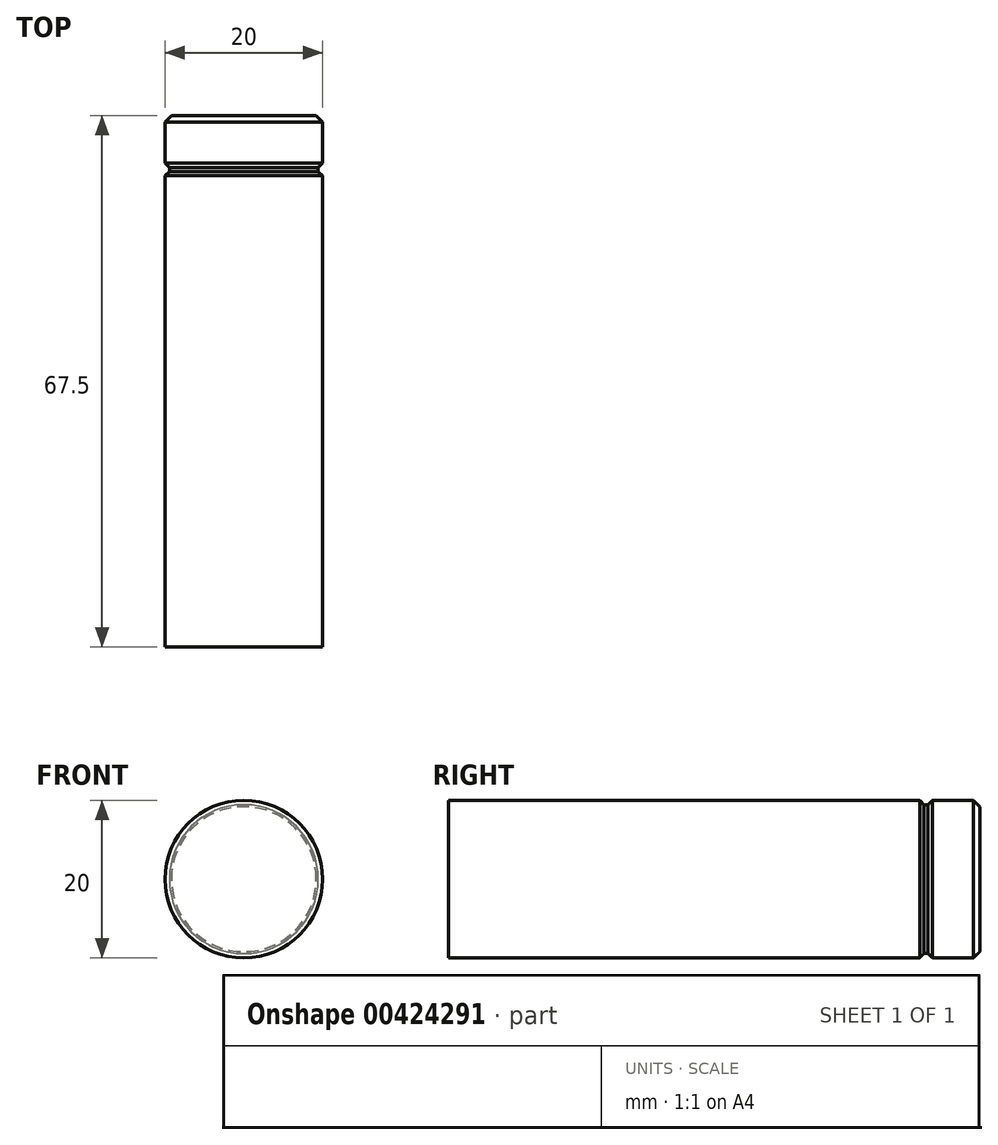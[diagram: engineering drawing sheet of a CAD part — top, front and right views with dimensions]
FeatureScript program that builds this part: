
annotation { "Feature Type Name" : "Feature", "Feature Type Description" : "" }
export const myFeature = defineFeature(function(context is Context, id is Id, definition is map)
    precondition{}
    {
        {
            var Q0;
            Q0=qCreatedBy(makeId("Front.planeOp"),FACE);
            var sketch = newSketch(context, id + "F0", { "sketchPlane" : qUnion([Q0])});
            skCircle(sketch, "E0", {"center": v(0, 0) * mm, "radius": 10 * mm});
            skSolve(sketch);
        }
        {
            var Q0;
            Q0=makeQuery(id+"F0.imprint","IMPRINT",FACE,{"disambiguationData":[TD([[makeQuery(id+"F0.imprint","IMPRINT",EDGE,{"derivedFrom":sQuery(id+"F0.wireOp",EDGE,"E0")}),1.0]])]});
            extrude(context, id + "F1", {"entities" : qUnion([Q0]), "oppositeDirection" : true, "depth" : 67.5 * mm});
        }
        {
            var Q0;
            Q0=qCreatedBy(makeId("Right.planeOp"),FACE);
            var sketch = newSketch(context, id + "F2", { "sketchPlane" : qUnion([Q0])});
            skLineSegment(sketch, "E1.bottom", {"start": v(60.9, 9.46) * mm, "end": v(60.4, 9.46) * mm});
            skLineSegment(sketch, "E2", {"start": v(60.4, 9.46) * mm, "end": v(59.83, 10.02) * mm});
            skLineSegment(sketch, "E3", {"start": v(60.9, 9.46) * mm, "end": v(61.47, 10.02) * mm});
            skLineSegment(sketch, "E4", {"start": v(61.47, 10.02) * mm, "end": v(59.83, 10.02) * mm});
            skLineSegment(sketch, "E5.MirrorCS", {"start": v(60.9, -9.46) * mm, "end": v(60.4, -9.46) * mm});
            skLineSegment(sketch, "E6.MirrorCS", {"start": v(61.47, -10.02) * mm, "end": v(59.83, -10.02) * mm});
            skLineSegment(sketch, "E7.MirrorCS", {"start": v(60.9, -9.46) * mm, "end": v(61.47, -10.02) * mm});
            skLineSegment(sketch, "E8.MirrorCS", {"start": v(60.4, -9.46) * mm, "end": v(59.83, -10.02) * mm});
            skSolve(sketch);
        }
        {
            var Q0;
            Q0=makeQuery(id+"F2.imprint","IMPRINT",FACE,{"disambiguationData":[TD([[makeQuery(id+"F2.imprint","IMPRINT",EDGE,{"derivedFrom":sQuery(id+"F2.wireOp",EDGE,"E1.bottom")}),-1.0]])]});
            var Q1;
            Q1=makeQuery(id+"F2.imprint","IMPRINT",FACE,{"disambiguationData":[TD([[makeQuery(id+"F2.imprint","IMPRINT",EDGE,{"derivedFrom":sQuery(id+"F2.wireOp",EDGE,"E8.MirrorCS")}),1.0]])]});
            var Q2;
            Q2=sQuery(id+"F2.wireOp",EDGE,"E5.MirrorCS");
            var Q3;
            Q3=sQuery(id+"F2.wireOp",EDGE,"E8.MirrorCS");
            var Q4;
            Q4=sQuery(id+"F2.wireOp",EDGE,"E7.MirrorCS");
            var Q5;
            Q5=sQuery(id+"F2.wireOp",EDGE,"E6.MirrorCS");
            var Q6;
            Q6=sQuery(id+"F2.wireOp",EDGE,"E1.bottom");
            var Q7;
            Q7=sQuery(id+"F2.wireOp",EDGE,"E2");
            var Q8;
            Q8=sQuery(id+"F2.wireOp",EDGE,"E4");
            var Q9;
            Q9=sQuery(id+"F2.wireOp",EDGE,"E3");
            var Q10;
            Q10=makeQuery(id+"F1.opExtrude","SWEPT_FACE",FACE,{"disambiguationData":[OSD([sQuery(id+"F0.wireOp",EDGE,"E0")])]});
            revolve(context, id + "F3", {"operationType" : NewBodyOperationType.REMOVE, "entities" : qUnion([Q0, Q1]), "surfaceEntities" : qUnion([Q2, Q3, Q4, Q5, Q6, Q7, Q8, Q9]), "axis" : qUnion([Q10]), "revolveType" : RevolveType.FULL});
        }
        {
            var Q0;
            Q0=makeQuery(id+"F1.opExtrude","CAP_EDGE",EDGE,{"disambiguationData":[OSD([sQuery(id+"F0.wireOp",EDGE,"E0")])],"isStart":false});
            chamfer(context, id + "F4", {"entities" : qUnion([Q0]), "chamferType" : ChamferType.OFFSET_ANGLE, "width" : 0.8 * mm, "oppositeDirection" : false, "angle" : 45 * degree, "tangentPropagation" : true});
        }
    });
